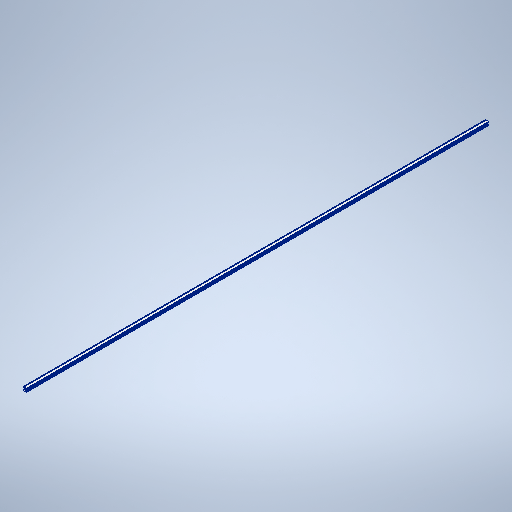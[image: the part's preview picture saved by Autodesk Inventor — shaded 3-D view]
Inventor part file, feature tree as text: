
AUTODESK INVENTOR PART (.ipt)
format: ipt  version: 2025.2 (Build 292293000, 293)  size: 308,736 bytes
history: native  units: mm
features: mirror x2, other x1, extrude x1, sketch x1
ambient origin geometry x8: Origin, YZ Plane, XZ Plane, XY Plane, X Axis, Y Axis, Z Axis, Center Point
bodies: Body1 (feature_tree)
feature tree (5):
  other  "Sólido1"
  extrude  "Extrusão1"  Depth=6.2mm
  mirror  "Espelhar1"
  mirror  "Espelhar2"
  sketch  "Esboço1"  dims[d0=15.0mm d1=6.2mm d2=7.5mm d4=2.0mm d5=6.0mm d7=3.1mm d8=2000.0mm d9=0.0mm d10=0.5mm d11=0.5mm d12=0.2mm d13=0.5mm]
